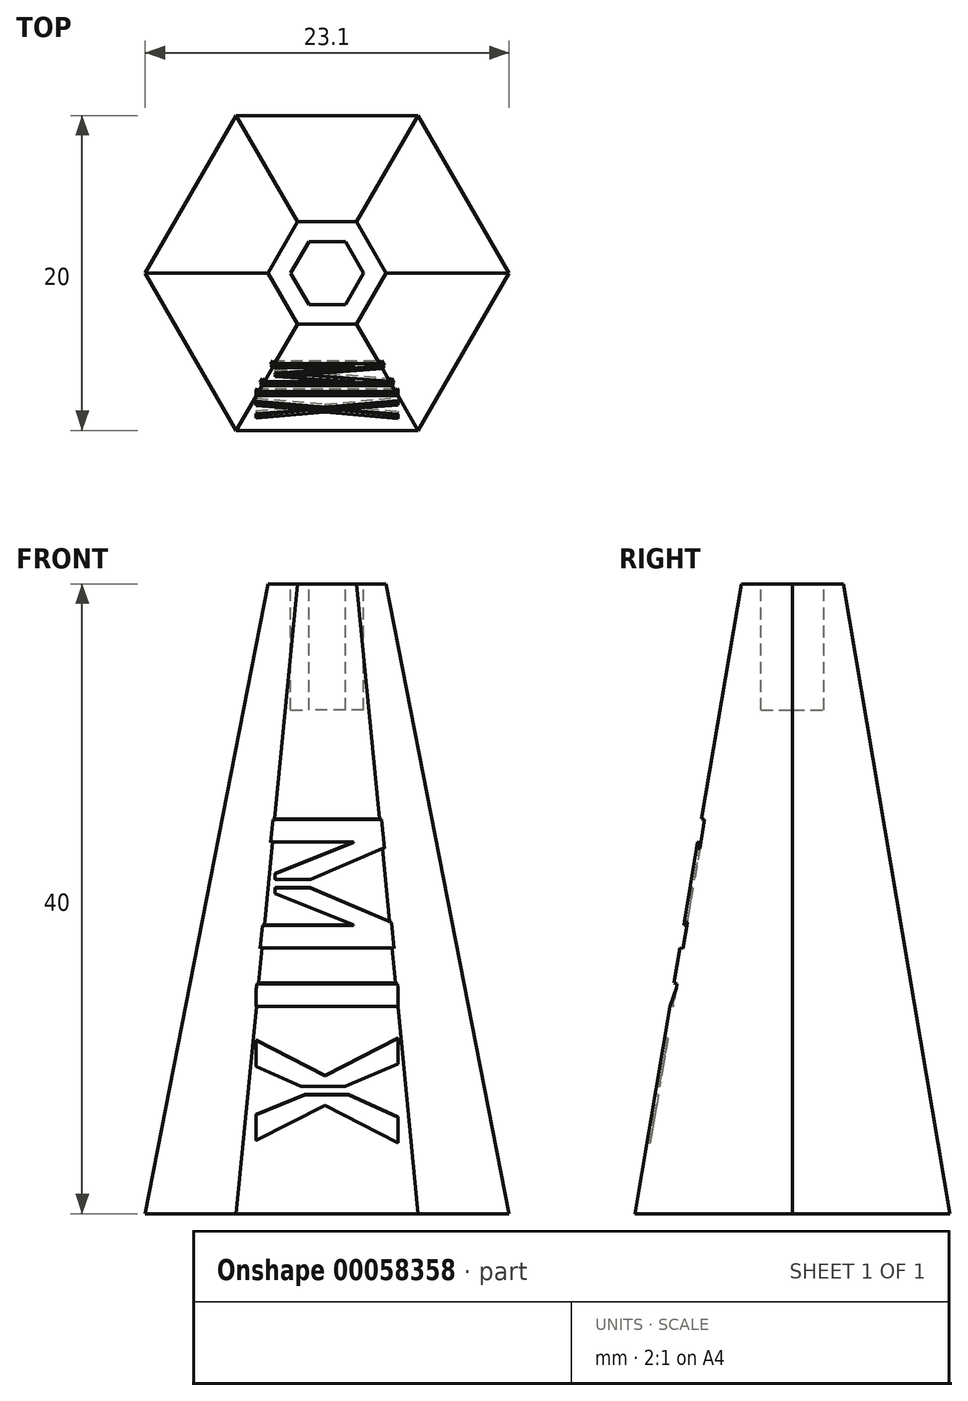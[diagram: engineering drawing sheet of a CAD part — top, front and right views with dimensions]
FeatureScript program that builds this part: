
annotation { "Feature Type Name" : "Feature", "Feature Type Description" : "" }
export const myFeature = defineFeature(function(context is Context, id is Id, definition is map)
    precondition{}
    {
        {
            var Q0;
            Q0=qCreatedBy(makeId("Top.planeOp"),FACE);
            var sketch = newSketch(context, id + "F0", { "sketchPlane" : qUnion([Q0])});
            skCircle(sketch, "E0.cCircle", {"center": v(0, 0) * mm, "radius": 10 * mm, "construction": true});
            skLineSegment(sketch, "E0.0", {"start": v(-5.77, -10) * mm, "end": v(-11.55, 0) * mm});
            skLineSegment(sketch, "E0.1", {"start": v(-11.55, 0) * mm, "end": v(-5.77, 10) * mm});
            skLineSegment(sketch, "E0.2", {"start": v(-5.77, 10) * mm, "end": v(5.77, 10) * mm});
            skLineSegment(sketch, "E0.3", {"start": v(5.77, 10) * mm, "end": v(11.55, 0) * mm});
            skLineSegment(sketch, "E0.4", {"start": v(11.55, 0) * mm, "end": v(5.77, -10) * mm});
            skLineSegment(sketch, "E0.5", {"start": v(5.77, -10) * mm, "end": v(-5.77, -10) * mm});
            skPoint(sketch, "E0.0.midPoint", {"position": v(-8.66, -5) * mm});
            skSolve(sketch);
        }
        {
            assignVariable(context, id + "F1", {"name" : "Height", "anyValue" : 40});
        }
        {
            var Q0;
            Q0=qCreatedBy(makeId("Top.planeOp"),FACE);
            cPlane(context, id + "F2", {"entities" : qUnion([Q0]), "cplaneType" : CPlaneType.OFFSET, "offset" : (getVariable(context, 'Height')) * mm, "width" : 150 * mm, "height" : 150 * mm});
        }
        {
            var Q0;
            Q0=qCreatedBy(id+"F2.planeOp",FACE);
            var sketch = newSketch(context, id + "F3", { "sketchPlane" : qUnion([Q0])});
            skCircle(sketch, "E1.cCircle", {"center": v(0, 0) * mm, "radius": 3.25 * mm, "construction": true});
            skLineSegment(sketch, "E1.0", {"start": v(-1.88, -3.25) * mm, "end": v(-3.75, 0) * mm});
            skLineSegment(sketch, "E1.1", {"start": v(-3.75, 0) * mm, "end": v(-1.88, 3.25) * mm});
            skLineSegment(sketch, "E1.2", {"start": v(-1.88, 3.25) * mm, "end": v(1.88, 3.25) * mm});
            skLineSegment(sketch, "E1.3", {"start": v(1.88, 3.25) * mm, "end": v(3.75, 0) * mm});
            skLineSegment(sketch, "E1.4", {"start": v(3.75, 0) * mm, "end": v(1.88, -3.25) * mm});
            skLineSegment(sketch, "E1.5", {"start": v(1.88, -3.25) * mm, "end": v(-1.88, -3.25) * mm});
            skPoint(sketch, "E1.0.midPoint", {"position": v(-2.81, -1.63) * mm});
            skSolve(sketch);
        }
        {
            var Q0;
            Q0=makeQuery(id+"F0.imprint","IMPRINT",FACE,{"disambiguationData":[TD([[makeQuery(id+"F0.imprint","IMPRINT",EDGE,{"derivedFrom":sQuery(id+"F0.wireOp",EDGE,"E0.0")}),-1.0]])]});
            var Q1;
            Q1=makeQuery(id+"F3.imprint","IMPRINT",FACE,{"disambiguationData":[TD([[makeQuery(id+"F3.imprint","IMPRINT",EDGE,{"derivedFrom":sQuery(id+"F3.wireOp",EDGE,"E1.0")}),-1.0]])]});
            loft(context, id + "F4", {"sheetProfilesArray" : [{ "sheetProfileEntities" : qUnion([Q0]) }, { "sheetProfileEntities" : qUnion([Q1]) }]});
        }
        {
            var Q0;
            Q0=qCreatedBy(id+"F2.planeOp",FACE);
            var sketch = newSketch(context, id + "F5", { "sketchPlane" : qUnion([Q0])});
            skCircle(sketch, "E2.cCircle", {"center": v(0, 0) * mm, "radius": 2 * mm, "construction": true});
            skLineSegment(sketch, "E2.0", {"start": v(-2.3, 0) * mm, "end": v(-1.15, 2) * mm});
            skLineSegment(sketch, "E2.1", {"start": v(-1.15, 2) * mm, "end": v(1.15, 2) * mm});
            skLineSegment(sketch, "E2.2", {"start": v(1.15, 2) * mm, "end": v(2.3, 0) * mm});
            skLineSegment(sketch, "E2.3", {"start": v(2.3, 0) * mm, "end": v(1.15, -2) * mm});
            skLineSegment(sketch, "E2.4", {"start": v(1.15, -2) * mm, "end": v(-1.15, -2) * mm});
            skLineSegment(sketch, "E2.5", {"start": v(-1.15, -2) * mm, "end": v(-2.3, 0) * mm});
            skPoint(sketch, "E2.0.midPoint", {"position": v(-1.73, 1) * mm});
            skSolve(sketch);
        }
        {
            var Q0;
            Q0=makeQuery(id+"F5.imprint","IMPRINT",FACE,{"disambiguationData":[TD([[makeQuery(id+"F5.imprint","IMPRINT",EDGE,{"derivedFrom":sQuery(id+"F5.wireOp",EDGE,"E2.0")}),-1.0]])]});
            extrude(context, id + "F6", {"entities" : qUnion([Q0]), "operationType" : NewBodyOperationType.REMOVE, "oppositeDirection" : true, "depth" : 8 * mm});
        }
        {
            var Q0;
            Q0=makeQuery(id+"F4.opLoft","SWEPT_FACE",FACE,{"disambiguationData":[OSD([sQuery(id+"F0.wireOp",EDGE,"E0.0"),sQuery(id+"F0.wireOp",EDGE,"E0.4"),sQuery(id+"F0.wireOp",EDGE,"E0.5"),sQuery(id+"F3.wireOp",EDGE,"E1.0"),sQuery(id+"F3.wireOp",EDGE,"E1.4"),sQuery(id+"F3.wireOp",EDGE,"E1.5")])]});
            var sketch = newSketch(context, id + "F7", { "sketchPlane" : qUnion([Q0])});
            skText(sketch, "E3", { "text": "MIX", "fontName": "AllertaStencil-Regular.ttf"});
            const initialGuessF7  = {"E3": [-0.00688, 0.0027, 1, 0, 0.009]};
            skSetInitialGuess(sketch, initialGuessF7);
            skSolve(sketch);
        }
        {
            var Q0;
            Q0 = qSketchRegion(id + "F7", true);
            extrude(context, id + "F8", {"entities" : qUnion([Q0]), "oppositeDirection" : true, "depth" : 0.2 * mm});
        }
        {
            var Q0;
            Q0=makeQuery(id+"F8.opExtrude","SWEPT_BODY",BODY,{"disambiguationData":[OSD([sQuery(id+"F7.wireOp",EDGE,"E3.sketch_text.stroke-0"),sQuery(id+"F7.wireOp",EDGE,"E3.sketch_text.stroke-1"),sQuery(id+"F7.wireOp",EDGE,"E3.sketch_text.stroke-2"),sQuery(id+"F7.wireOp",EDGE,"E3.sketch_text.stroke-3"),sQuery(id+"F7.wireOp",EDGE,"E3.sketch_text.stroke-4"),sQuery(id+"F7.wireOp",EDGE,"E3.sketch_text.stroke-5"),sQuery(id+"F7.wireOp",EDGE,"E3.sketch_text.stroke-6"),sQuery(id+"F7.wireOp",EDGE,"E3.sketch_text.stroke-7")])]});
            var Q1;
            Q1=makeQuery(id+"F8.opExtrude","SWEPT_BODY",BODY,{"disambiguationData":[OSD([sQuery(id+"F7.wireOp",EDGE,"E3.sketch_text.stroke-8"),sQuery(id+"F7.wireOp",EDGE,"E3.sketch_text.stroke-9"),sQuery(id+"F7.wireOp",EDGE,"E3.sketch_text.stroke-10"),sQuery(id+"F7.wireOp",EDGE,"E3.sketch_text.stroke-11"),sQuery(id+"F7.wireOp",EDGE,"E3.sketch_text.stroke-12"),sQuery(id+"F7.wireOp",EDGE,"E3.sketch_text.stroke-13"),sQuery(id+"F7.wireOp",EDGE,"E3.sketch_text.stroke-14"),sQuery(id+"F7.wireOp",EDGE,"E3.sketch_text.stroke-15")])]});
            var Q2;
            Q2=makeQuery(id+"F8.opExtrude","SWEPT_BODY",BODY,{"disambiguationData":[OSD([sQuery(id+"F7.wireOp",EDGE,"E3.sketch_text.stroke-16"),sQuery(id+"F7.wireOp",EDGE,"E3.sketch_text.stroke-17"),sQuery(id+"F7.wireOp",EDGE,"E3.sketch_text.stroke-18"),sQuery(id+"F7.wireOp",EDGE,"E3.sketch_text.stroke-19")])]});
            var Q3;
            Q3=makeQuery(id+"F8.opExtrude","SWEPT_BODY",BODY,{"disambiguationData":[OSD([sQuery(id+"F7.wireOp",EDGE,"E3.sketch_text.stroke-20"),sQuery(id+"F7.wireOp",EDGE,"E3.sketch_text.stroke-21"),sQuery(id+"F7.wireOp",EDGE,"E3.sketch_text.stroke-22"),sQuery(id+"F7.wireOp",EDGE,"E3.sketch_text.stroke-23"),sQuery(id+"F7.wireOp",EDGE,"E3.sketch_text.stroke-24"),sQuery(id+"F7.wireOp",EDGE,"E3.sketch_text.stroke-25"),sQuery(id+"F7.wireOp",EDGE,"E3.sketch_text.stroke-26")])]});
            var Q4;
            Q4=makeQuery(id+"F8.opExtrude","SWEPT_BODY",BODY,{"disambiguationData":[OSD([sQuery(id+"F7.wireOp",EDGE,"E3.sketch_text.stroke-27"),sQuery(id+"F7.wireOp",EDGE,"E3.sketch_text.stroke-28"),sQuery(id+"F7.wireOp",EDGE,"E3.sketch_text.stroke-29"),sQuery(id+"F7.wireOp",EDGE,"E3.sketch_text.stroke-30"),sQuery(id+"F7.wireOp",EDGE,"E3.sketch_text.stroke-31"),sQuery(id+"F7.wireOp",EDGE,"E3.sketch_text.stroke-32"),sQuery(id+"F7.wireOp",EDGE,"E3.sketch_text.stroke-33")])]});
            var Q5;
            Q5=makeQuery(id+"F8.opExtrude","SWEPT_EDGE",EDGE,{"disambiguationData":[OSD([sQuery(id+"F7.wireOp",EDGE,"E3.sketch_text.stroke-18"),sQuery(id+"F7.wireOp",EDGE,"E3.sketch_text.stroke-19")])]});
            transform(context, id + "F9", {"entities" : qUnion([Q0, Q1, Q2, Q3, Q4]), "transformType" : TransformType.ROTATION, "transformAxis" : qUnion([Q5]), "angle" : 270 * degree, "makeCopy" : false});
        }
        {
            var Q0;
            Q0=makeQuery(id+"F8.opExtrude","SWEPT_BODY",BODY,{"disambiguationData":[OSD([sQuery(id+"F7.wireOp",EDGE,"E3.sketch_text.stroke-0"),sQuery(id+"F7.wireOp",EDGE,"E3.sketch_text.stroke-1"),sQuery(id+"F7.wireOp",EDGE,"E3.sketch_text.stroke-2"),sQuery(id+"F7.wireOp",EDGE,"E3.sketch_text.stroke-3"),sQuery(id+"F7.wireOp",EDGE,"E3.sketch_text.stroke-4"),sQuery(id+"F7.wireOp",EDGE,"E3.sketch_text.stroke-5"),sQuery(id+"F7.wireOp",EDGE,"E3.sketch_text.stroke-6"),sQuery(id+"F7.wireOp",EDGE,"E3.sketch_text.stroke-7")])]});
            var Q1;
            Q1=makeQuery(id+"F8.opExtrude","SWEPT_BODY",BODY,{"disambiguationData":[OSD([sQuery(id+"F7.wireOp",EDGE,"E3.sketch_text.stroke-8"),sQuery(id+"F7.wireOp",EDGE,"E3.sketch_text.stroke-9"),sQuery(id+"F7.wireOp",EDGE,"E3.sketch_text.stroke-10"),sQuery(id+"F7.wireOp",EDGE,"E3.sketch_text.stroke-11"),sQuery(id+"F7.wireOp",EDGE,"E3.sketch_text.stroke-12"),sQuery(id+"F7.wireOp",EDGE,"E3.sketch_text.stroke-13"),sQuery(id+"F7.wireOp",EDGE,"E3.sketch_text.stroke-14"),sQuery(id+"F7.wireOp",EDGE,"E3.sketch_text.stroke-15")])]});
            var Q2;
            Q2=makeQuery(id+"F8.opExtrude","SWEPT_BODY",BODY,{"disambiguationData":[OSD([sQuery(id+"F7.wireOp",EDGE,"E3.sketch_text.stroke-16"),sQuery(id+"F7.wireOp",EDGE,"E3.sketch_text.stroke-17"),sQuery(id+"F7.wireOp",EDGE,"E3.sketch_text.stroke-18"),sQuery(id+"F7.wireOp",EDGE,"E3.sketch_text.stroke-19")])]});
            var Q3;
            Q3=makeQuery(id+"F8.opExtrude","SWEPT_BODY",BODY,{"disambiguationData":[OSD([sQuery(id+"F7.wireOp",EDGE,"E3.sketch_text.stroke-20"),sQuery(id+"F7.wireOp",EDGE,"E3.sketch_text.stroke-21"),sQuery(id+"F7.wireOp",EDGE,"E3.sketch_text.stroke-22"),sQuery(id+"F7.wireOp",EDGE,"E3.sketch_text.stroke-23"),sQuery(id+"F7.wireOp",EDGE,"E3.sketch_text.stroke-24"),sQuery(id+"F7.wireOp",EDGE,"E3.sketch_text.stroke-25"),sQuery(id+"F7.wireOp",EDGE,"E3.sketch_text.stroke-26")])]});
            var Q4;
            Q4=makeQuery(id+"F8.opExtrude","SWEPT_BODY",BODY,{"disambiguationData":[OSD([sQuery(id+"F7.wireOp",EDGE,"E3.sketch_text.stroke-27"),sQuery(id+"F7.wireOp",EDGE,"E3.sketch_text.stroke-28"),sQuery(id+"F7.wireOp",EDGE,"E3.sketch_text.stroke-29"),sQuery(id+"F7.wireOp",EDGE,"E3.sketch_text.stroke-30"),sQuery(id+"F7.wireOp",EDGE,"E3.sketch_text.stroke-31"),sQuery(id+"F7.wireOp",EDGE,"E3.sketch_text.stroke-32"),sQuery(id+"F7.wireOp",EDGE,"E3.sketch_text.stroke-33")])]});
            transform(context, id + "F10", {"entities" : qUnion([Q0, Q1, Q2, Q3, Q4]), "transformType" : TransformType.TRANSLATION_3D, "dx" : -1.82 * mm, "dy" : 0 * mm, "dz" : 0 * mm, "makeCopy" : false});
        }
        {
            var Q0;
            Q0=makeQuery(id+"F8.opExtrude","SWEPT_BODY",BODY,{"disambiguationData":[OSD([sQuery(id+"F7.wireOp",EDGE,"E3.sketch_text.stroke-0"),sQuery(id+"F7.wireOp",EDGE,"E3.sketch_text.stroke-1"),sQuery(id+"F7.wireOp",EDGE,"E3.sketch_text.stroke-2"),sQuery(id+"F7.wireOp",EDGE,"E3.sketch_text.stroke-3"),sQuery(id+"F7.wireOp",EDGE,"E3.sketch_text.stroke-4"),sQuery(id+"F7.wireOp",EDGE,"E3.sketch_text.stroke-5"),sQuery(id+"F7.wireOp",EDGE,"E3.sketch_text.stroke-6"),sQuery(id+"F7.wireOp",EDGE,"E3.sketch_text.stroke-7")])]});
            var Q1;
            Q1=makeQuery(id+"F8.opExtrude","SWEPT_BODY",BODY,{"disambiguationData":[OSD([sQuery(id+"F7.wireOp",EDGE,"E3.sketch_text.stroke-8"),sQuery(id+"F7.wireOp",EDGE,"E3.sketch_text.stroke-9"),sQuery(id+"F7.wireOp",EDGE,"E3.sketch_text.stroke-10"),sQuery(id+"F7.wireOp",EDGE,"E3.sketch_text.stroke-11"),sQuery(id+"F7.wireOp",EDGE,"E3.sketch_text.stroke-12"),sQuery(id+"F7.wireOp",EDGE,"E3.sketch_text.stroke-13"),sQuery(id+"F7.wireOp",EDGE,"E3.sketch_text.stroke-14"),sQuery(id+"F7.wireOp",EDGE,"E3.sketch_text.stroke-15")])]});
            var Q2;
            Q2=makeQuery(id+"F8.opExtrude","SWEPT_BODY",BODY,{"disambiguationData":[OSD([sQuery(id+"F7.wireOp",EDGE,"E3.sketch_text.stroke-27"),sQuery(id+"F7.wireOp",EDGE,"E3.sketch_text.stroke-28"),sQuery(id+"F7.wireOp",EDGE,"E3.sketch_text.stroke-29"),sQuery(id+"F7.wireOp",EDGE,"E3.sketch_text.stroke-30"),sQuery(id+"F7.wireOp",EDGE,"E3.sketch_text.stroke-31"),sQuery(id+"F7.wireOp",EDGE,"E3.sketch_text.stroke-32"),sQuery(id+"F7.wireOp",EDGE,"E3.sketch_text.stroke-33")])]});
            var Q3;
            Q3=makeQuery(id+"F8.opExtrude","SWEPT_BODY",BODY,{"disambiguationData":[OSD([sQuery(id+"F7.wireOp",EDGE,"E3.sketch_text.stroke-20"),sQuery(id+"F7.wireOp",EDGE,"E3.sketch_text.stroke-21"),sQuery(id+"F7.wireOp",EDGE,"E3.sketch_text.stroke-22"),sQuery(id+"F7.wireOp",EDGE,"E3.sketch_text.stroke-23"),sQuery(id+"F7.wireOp",EDGE,"E3.sketch_text.stroke-24"),sQuery(id+"F7.wireOp",EDGE,"E3.sketch_text.stroke-25"),sQuery(id+"F7.wireOp",EDGE,"E3.sketch_text.stroke-26")])]});
            var Q4;
            Q4=makeQuery(id+"F8.opExtrude","SWEPT_BODY",BODY,{"disambiguationData":[OSD([sQuery(id+"F7.wireOp",EDGE,"E3.sketch_text.stroke-16"),sQuery(id+"F7.wireOp",EDGE,"E3.sketch_text.stroke-17"),sQuery(id+"F7.wireOp",EDGE,"E3.sketch_text.stroke-18"),sQuery(id+"F7.wireOp",EDGE,"E3.sketch_text.stroke-19")])]});
            var Q5;
            Q5=makeQuery(id+"F4.opLoft","SWEPT_BODY",BODY,{"disambiguationData":[OSD([makeQuery(id+"F0.imprint","IMPRINT",FACE,{"disambiguationData":[TD([[makeQuery(id+"F0.imprint","IMPRINT",EDGE,{"derivedFrom":sQuery(id+"F0.wireOp",EDGE,"E0.0")}),-1.0]])]}),makeQuery(id+"F3.imprint","IMPRINT",FACE,{"disambiguationData":[TD([[makeQuery(id+"F3.imprint","IMPRINT",EDGE,{"derivedFrom":sQuery(id+"F3.wireOp",EDGE,"E1.0")}),-1.0]])]})])]});
            booleanBodies(context, id + "F11", {"operationType" : BooleanOperationType.SUBTRACTION, "tools" : qUnion([Q0, Q1, Q2, Q3, Q4]), "targets" : qUnion([Q5])});
        }
    });
